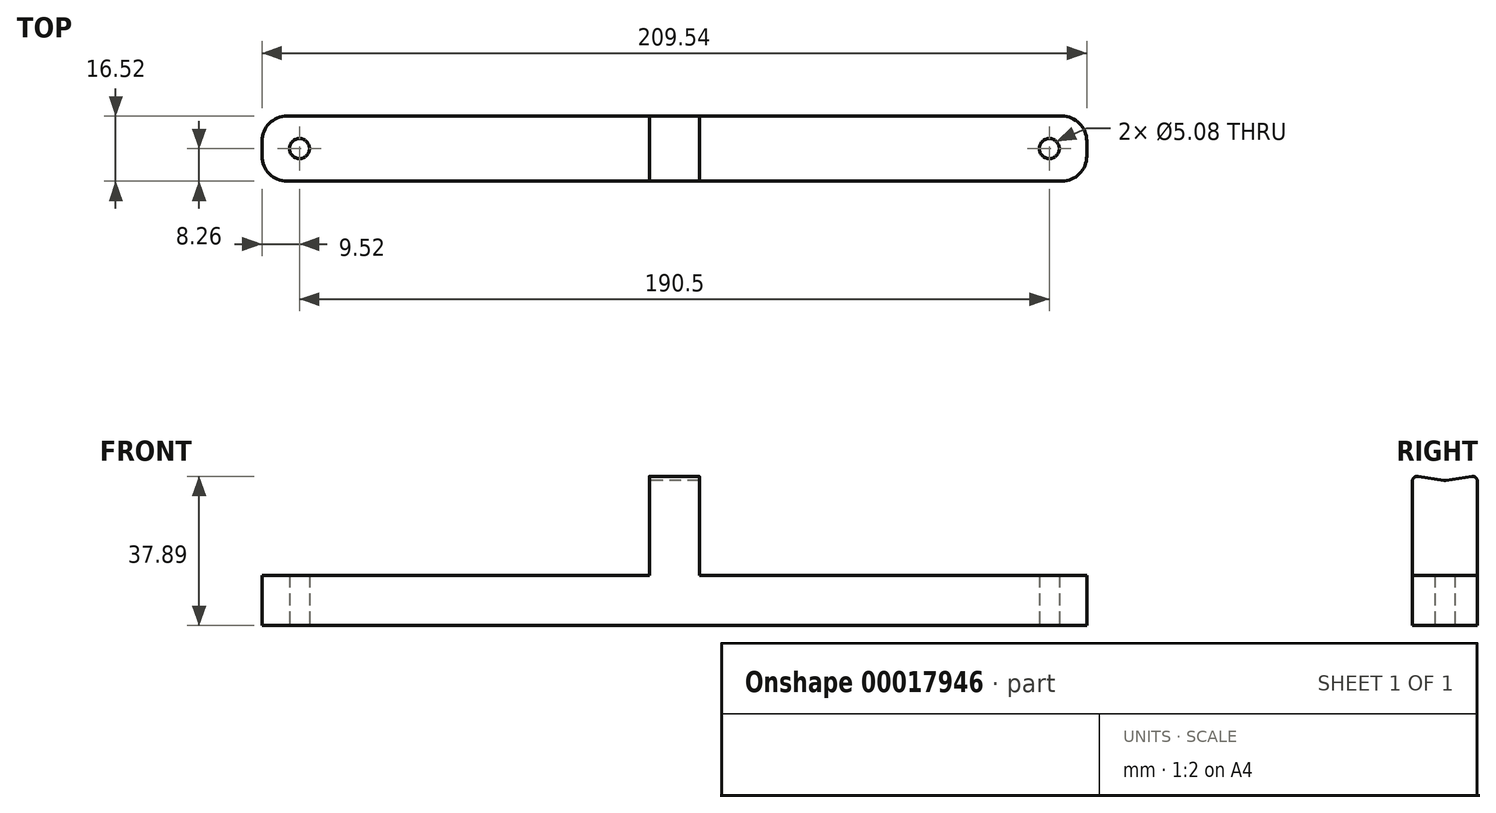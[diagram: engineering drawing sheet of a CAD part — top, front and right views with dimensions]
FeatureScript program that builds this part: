
annotation { "Feature Type Name" : "Feature", "Feature Type Description" : "" }
export const myFeature = defineFeature(function(context is Context, id is Id, definition is map)
    precondition{}
    {
        {
            var Q0;
            Q0=qCreatedBy(makeId("Top.planeOp"),FACE);
            var sketch = newSketch(context, id + "F0", { "sketchPlane" : qUnion([Q0])});
            skLineSegment(sketch, "E0.bottom", {"start": v(104.78, -8.25) * mm, "end": v(-104.78, -8.26) * mm});
            skLineSegment(sketch, "E0.top", {"start": v(104.78, 8.26) * mm, "end": v(-104.78, 8.25) * mm});
            skLineSegment(sketch, "E0.left", {"start": v(104.78, -8.25) * mm, "end": v(104.78, 8.26) * mm});
            skLineSegment(sketch, "E0.right", {"start": v(-104.78, -8.26) * mm, "end": v(-104.78, 8.25) * mm});
            skPoint(sketch, "E0.middle", {"position": v(0, 0) * mm});
            skCircle(sketch, "E1", {"center": v(-95.25, 0) * mm, "radius": 2.54 * mm});
            skCircle(sketch, "E2.MirrorC", {"center": v(95.25, 0) * mm, "radius": 2.54 * mm});
            skSolve(sketch);
        }
        {
            var Q0;
            Q0 = qSketchRegion(id + "F0", true);
            extrude(context, id + "F1", {"entities" : qUnion([Q0]), "depth" : 12.7 * mm, "offsetDistance" : 25.4 * mm});
        }
        {
            var Q0;
            Q0=makeQuery(id+"F1.opExtrude","SWEPT_EDGE",EDGE,{"disambiguationData":[OSD([sQuery(id+"F0.wireOp",EDGE,"E0.top"),sQuery(id+"F0.wireOp",EDGE,"E0.right")])]});
            var Q1;
            Q1=makeQuery(id+"F1.opExtrude","SWEPT_EDGE",EDGE,{"disambiguationData":[OSD([sQuery(id+"F0.wireOp",EDGE,"E0.bottom"),sQuery(id+"F0.wireOp",EDGE,"E0.right")])]});
            var Q2;
            Q2=makeQuery(id+"F1.opExtrude","SWEPT_EDGE",EDGE,{"disambiguationData":[OSD([sQuery(id+"F0.wireOp",EDGE,"E0.bottom"),sQuery(id+"F0.wireOp",EDGE,"E0.left")])]});
            var Q3;
            Q3=makeQuery(id+"F1.opExtrude","SWEPT_EDGE",EDGE,{"disambiguationData":[OSD([sQuery(id+"F0.wireOp",EDGE,"E0.top"),sQuery(id+"F0.wireOp",EDGE,"E0.left")])]});
            fillet(context, id + "F2", {"entities" : qUnion([Q0, Q1, Q2, Q3]), "tangentPropagation" : true, "radius" : 6.35 * mm, "defaultsChanged" : true, "vertexSettings" : [], "allowEdgeOverflow" : false});
        }
        {
            var Q0;
            Q0=makeQuery(id+"F1.opExtrude","CAP_FACE",FACE,{"disambiguationData":[OSD([sQuery(id+"F0.wireOp",EDGE,"E0.bottom"),sQuery(id+"F0.wireOp",EDGE,"E0.top"),sQuery(id+"F0.wireOp",EDGE,"E0.left"),sQuery(id+"F0.wireOp",EDGE,"E0.right"),sQuery(id+"F0.wireOp",EDGE,"E1"),sQuery(id+"F0.wireOp",EDGE,"E2.MirrorC")])],"isStart":false});
            var sketch = newSketch(context, id + "F3", { "sketchPlane" : qUnion([Q0])});
            skLineSegment(sketch, "E3.bottom", {"start": v(-6.35, 8.26) * mm, "end": v(6.35, 8.26) * mm});
            skLineSegment(sketch, "E3.top", {"start": v(-6.35, -8.26) * mm, "end": v(6.35, -8.26) * mm});
            skLineSegment(sketch, "E3.left", {"start": v(-6.35, 8.26) * mm, "end": v(-6.35, -8.26) * mm});
            skLineSegment(sketch, "E3.right", {"start": v(6.35, 8.26) * mm, "end": v(6.35, -8.26) * mm});
            skPoint(sketch, "E3.middle", {"position": v(0, 0) * mm});
            skSolve(sketch);
        }
        {
            var Q0;
            Q0 = qSketchRegion(id + "F3", true);
            extrude(context, id + "F4", {"entities" : qUnion([Q0]), "operationType" : NewBodyOperationType.ADD, "depth" : 25.4 * mm, "offsetDistance" : 25.4 * mm});
        }
        {
            var Q0;
            Q0=makeQuery(id+"F4.opExtrude","SWEPT_FACE",FACE,{"disambiguationData":[OSD([sQuery(id+"F3.wireOp",EDGE,"E3.right")])]});
            var sketch = newSketch(context, id + "F5", { "sketchPlane" : qUnion([Q0])});
            skLineSegment(sketch, "E4", {"start": v(-8.26, 38.1) * mm, "end": v(0, 36.83) * mm});
            skLineSegment(sketch, "E5", {"start": v(0, 36.83) * mm, "end": v(8.26, 38.1) * mm});
            skSolve(sketch);
        }
        {
            var Q0;
            Q0=makeQuery(id+"F5.imprint","IMPRINT",FACE,{"disambiguationData":[TD([[makeQuery(id+"F5.imprint","IMPRINT",EDGE,{"derivedFrom":sQuery(id+"F5.wireOp",EDGE,"u2JtxXhR-IWcC-k2TD-AlXt-rrE2Rt1QJ371")}),1.0]])]});
            var Q1;
            Q1=makeQuery(id+"F5.imprint","IMPRINT",FACE,{"disambiguationData":[TD([[makeQuery(id+"F5.imprint","IMPRINT",EDGE,{"derivedFrom":sQuery(id+"F5.wireOp",EDGE,"E4")}),1.0]])]});
            extrude(context, id + "F6", {"entities" : qUnion([Q0, Q1]), "operationType" : NewBodyOperationType.REMOVE, "oppositeDirection" : true, "depth" : 25.4 * mm, "offsetDistance" : 25.4 * mm});
        }
        {
            var Q0;
            {var subQ0=sQuery(id+"F3.wireOp",EDGE,"E3.top");Q0=makeQuery(id+"F6.boolean.opBoolean","MERGE",EDGE,{"derivedFrom":[makeQuery(id+"F4.opExtrude","CAP_EDGE",EDGE,{"disambiguationData":[OSD([subQ0])],"isStart":false})],"fromTools":[makeQuery(id+"F6.opExtrude","SWEPT_EDGE",EDGE,{"disambiguationData":[OSD([sQuery(id+"F0.wireOp",EDGE,"E0.bottom"),subQ0,sQuery(id+"F3.wireOp",EDGE,"E3.right"),sQuery(id+"F5.wireOp",EDGE,"E4")])]})]});}
            var Q1;
            {var subQ0=sQuery(id+"F3.wireOp",EDGE,"E3.bottom");Q1=makeQuery(id+"F6.boolean.opBoolean","MERGE",EDGE,{"derivedFrom":[makeQuery(id+"F4.opExtrude","CAP_EDGE",EDGE,{"disambiguationData":[OSD([subQ0])],"isStart":false})],"fromTools":[makeQuery(id+"F6.opExtrude","SWEPT_EDGE",EDGE,{"disambiguationData":[OSD([sQuery(id+"F0.wireOp",EDGE,"E0.top"),subQ0,sQuery(id+"F3.wireOp",EDGE,"E3.right"),sQuery(id+"F5.wireOp",EDGE,"E5")])]})]});}
            var Q2;
            Q2=makeQuery(id+"F6.boolean.opBoolean","COPY",EDGE,{"derivedFrom":makeQuery(id+"F6.opExtrude","SWEPT_EDGE",EDGE,{"disambiguationData":[OSD([sQuery(id+"F5.wireOp",EDGE,"E4"),sQuery(id+"F5.wireOp",EDGE,"E5")])]})});
            fillet(context, id + "F7", {"entities" : qUnion([Q0, Q1, Q2]), "tangentPropagation" : true, "radius" : 1.27 * mm, "defaultsChanged" : true, "vertexSettings" : [], "allowEdgeOverflow" : false});
        }
    });
